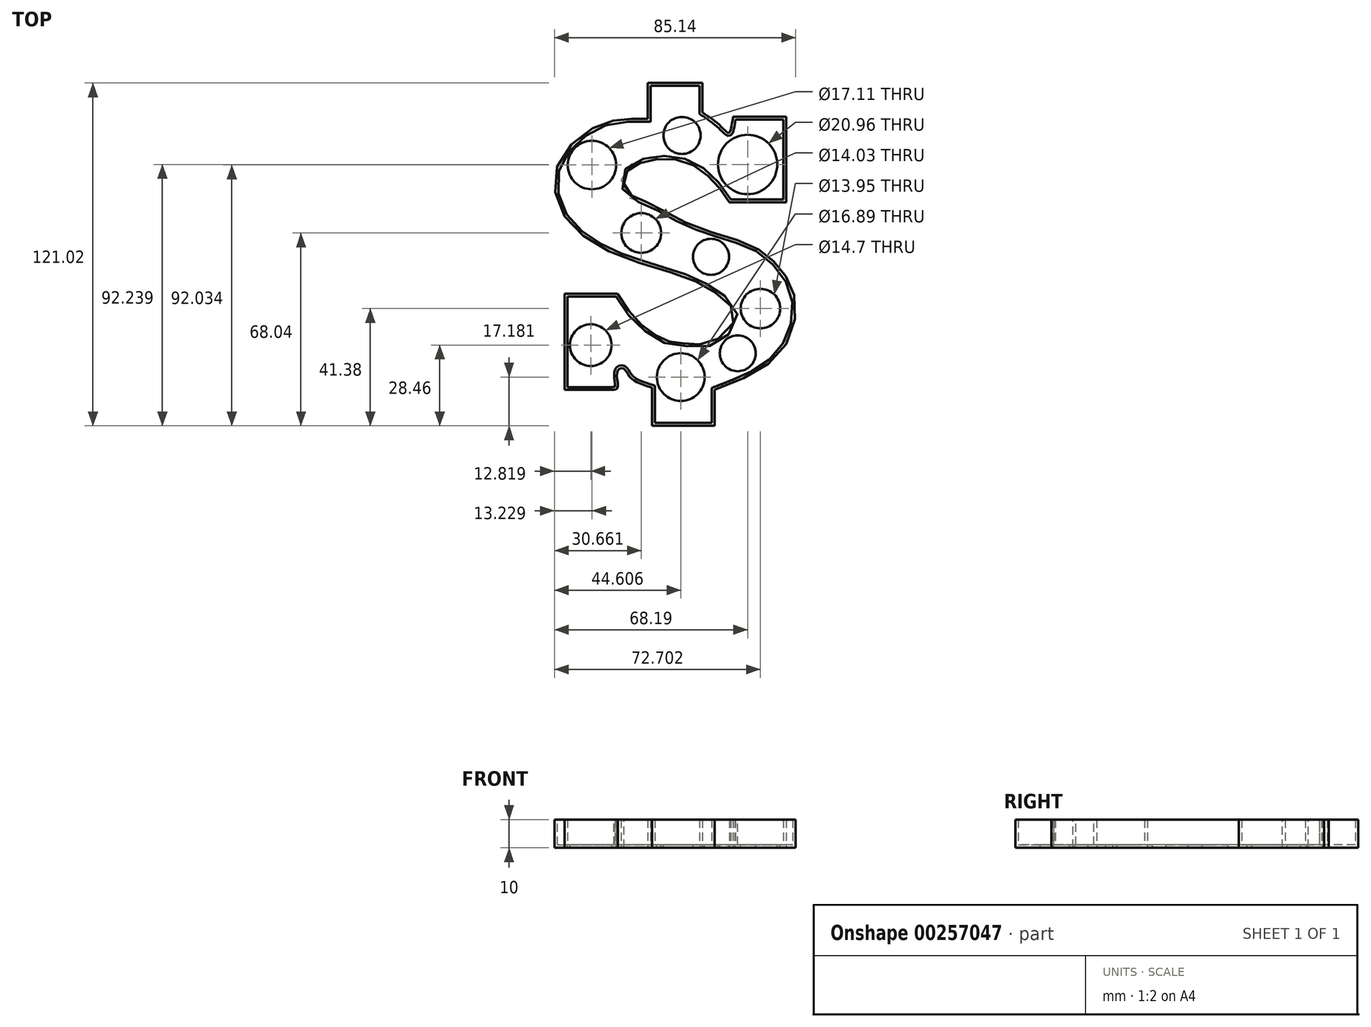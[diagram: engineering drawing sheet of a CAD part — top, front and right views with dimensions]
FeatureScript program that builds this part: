
annotation { "Feature Type Name" : "Feature", "Feature Type Description" : "" }
export const myFeature = defineFeature(function(context is Context, id is Id, definition is map)
    precondition{}
    {
        {
            var Q0;
            Q0=qCreatedBy(makeId("Top.planeOp"),FACE);
            var sketch = newSketch(context, id + "F0", { "sketchPlane" : qUnion([Q0])});
            skLineSegment(sketch, "E0", {"start": v(-8.22, 52.98) * mm, "end": v(11.07, 52.98) * mm});
            skLineSegment(sketch, "E1", {"start": v(11.07, 52.98) * mm, "end": v(11.07, 42.64) * mm});
            skLineSegment(sketch, "E2", {"start": v(-8.22, 52.98) * mm, "end": v(-8.22, 42.64) * mm});
            skLineSegment(sketch, "E3", {"start": v(21.96, 41) * mm, "end": v(40.65, 41) * mm});
            skLineSegment(sketch, "E4", {"start": v(40.65, 41) * mm, "end": v(40.65, 10.82) * mm});
            skLineSegment(sketch, "E5", {"start": v(40.65, 10.82) * mm, "end": v(20.61, 10.82) * mm});
            skLineSegment(sketch, "E6", {"start": v(-6.71, -54.62) * mm, "end": v(-6.71, -68.04) * mm});
            skLineSegment(sketch, "E7", {"start": v(-6.71, -68.04) * mm, "end": v(15.38, -68.04) * mm});
            skLineSegment(sketch, "E8", {"start": v(15.38, -68.04) * mm, "end": v(15.38, -55.37) * mm});
            skLineSegment(sketch, "E9", {"start": v(-20.87, -55.37) * mm, "end": v(-37.56, -55.37) * mm});
            skLineSegment(sketch, "E10", {"start": v(-37.56, -55.37) * mm, "end": v(-37.56, -21.41) * mm});
            skLineSegment(sketch, "E11", {"start": v(-37.56, -21.41) * mm, "end": v(-18.87, -21.41) * mm});
            skLineSegment(sketch, "E12", {"start": v(-8.22, 42.64) * mm, "end": v(-8.22, 40.28) * mm});
            skFitSpline(sketch, "E13", {"points": [v(-8.22, 40.28) * mm, v(-15.6, 40.28) * mm, v(-26.67, 37.56) * mm, v(-39.92, 24.13) * mm, v(-38.1, 6.9) * mm, v(-21.23, -6.71) * mm, v(4.9, -15.6) * mm, v(17.78, -22.5) * mm, v(22.5, -30.12) * mm, v(14.15, -38.65) * mm, v(5.8, -39.01) * mm, v(0, -38.47) * mm, v(-5.26, -36.1) * mm, v(-12.52, -30.3) * mm, v(-18.87, -21.41) * mm], "startDerivative": vector(-119.86, 3.94) * mm, "endDerivative": vector(-86.42, 138.88) * mm});
            skFitSpline(sketch, "E14", {"points": [v(11.07, 42.64) * mm, v(17.96, 37.38) * mm, v(20.5, 35.38) * mm, v(21.41, 37.92) * mm, v(21.96, 41) * mm], "startDerivative": vector(20.98, -14.44) * mm, "endDerivative": vector(2.34, 13.22) * mm});
            skFitSpline(sketch, "E15", {"points": [v(20.61, 10.82) * mm, v(15.04, 18.3) * mm, v(7.24, 24.26) * mm, v(-3.46, 26.25) * mm, v(-12.68, 23.9) * mm, v(-16.49, 19.82) * mm, v(-14.84, 13.96) * mm, v(-8.22, 10.82) * mm, v(7, 2.91) * mm, v(28.14, -4.28) * mm, v(37.94, -11.79) * mm, v(43.78, -23.23) * mm, v(38.5, -42.31) * mm, v(15.38, -55.37) * mm], "startDerivative": vector(-75.8, 124.36) * mm, "endDerivative": vector(-239.05, -90.17) * mm});
            skFitSpline(sketch, "E16", {"points": [v(-6.71, -54.62) * mm, v(-14.33, -50.99) * mm, v(-16.7, -47.9) * mm, v(-18.87, -48.63) * mm, v(-18.87, -54.62) * mm, v(-20.87, -55.37) * mm], "startDerivative": vector(-32.27, 10.38) * mm, "endDerivative": vector(-18.1, 0.06) * mm});
            skSolve(sketch);
        }
        {
            var Q0;
            Q0=makeQuery(id+"F0.imprint","IMPRINT",FACE,{"disambiguationData":[TD([[makeQuery(id+"F0.imprint","IMPRINT",EDGE,{"derivedFrom":sQuery(id+"F0.wireOp",EDGE,"E0")}),-1.0]])]});
            extrude(context, id + "F1", {"entities" : qUnion([Q0]), "depth" : 10 * mm});
        }
        {
            var Q0;
            Q0=makeQuery(id+"F1.opExtrude","CAP_FACE",FACE,{"disambiguationData":[OSD([sQuery(id+"F0.wireOp",EDGE,"E0"),sQuery(id+"F0.wireOp",EDGE,"E1"),sQuery(id+"F0.wireOp",EDGE,"E2"),sQuery(id+"F0.wireOp",EDGE,"E3"),sQuery(id+"F0.wireOp",EDGE,"E4"),sQuery(id+"F0.wireOp",EDGE,"E5"),sQuery(id+"F0.wireOp",EDGE,"E6"),sQuery(id+"F0.wireOp",EDGE,"E7"),sQuery(id+"F0.wireOp",EDGE,"E8"),sQuery(id+"F0.wireOp",EDGE,"E9"),sQuery(id+"F0.wireOp",EDGE,"E10"),sQuery(id+"F0.wireOp",EDGE,"E11"),sQuery(id+"F0.wireOp",EDGE,"E12"),sQuery(id+"F0.wireOp",EDGE,"E13"),sQuery(id+"F0.wireOp",EDGE,"E14"),sQuery(id+"F0.wireOp",EDGE,"E15"),sQuery(id+"F0.wireOp",EDGE,"E16")])],"isStart":false});
            shell(context, id + "F2", {"entities" : qUnion([Q0]), "thickness" : 1 * mm});
        }
        {
            var Q0;
            Q0=makeQuery(id+"F2.opShell","OFFSET_FACE",FACE,{"disambiguationData":[OSD([sQuery(id+"F0.wireOp",EDGE,"E0"),sQuery(id+"F0.wireOp",EDGE,"E1"),sQuery(id+"F0.wireOp",EDGE,"E2"),sQuery(id+"F0.wireOp",EDGE,"E3"),sQuery(id+"F0.wireOp",EDGE,"E4"),sQuery(id+"F0.wireOp",EDGE,"E5"),sQuery(id+"F0.wireOp",EDGE,"E6"),sQuery(id+"F0.wireOp",EDGE,"E7"),sQuery(id+"F0.wireOp",EDGE,"E8"),sQuery(id+"F0.wireOp",EDGE,"E9"),sQuery(id+"F0.wireOp",EDGE,"E10"),sQuery(id+"F0.wireOp",EDGE,"E11"),sQuery(id+"F0.wireOp",EDGE,"E12"),sQuery(id+"F0.wireOp",EDGE,"E13"),sQuery(id+"F0.wireOp",EDGE,"E14"),sQuery(id+"F0.wireOp",EDGE,"E15"),sQuery(id+"F0.wireOp",EDGE,"E16")])]});
            var sketch = newSketch(context, id + "F3", { "sketchPlane" : qUnion([Q0])});
            skCircle(sketch, "E17", {"center": v(27.07, 24.2) * mm, "radius": 10.48 * mm});
            skCircle(sketch, "E18", {"center": v(3.9, 34.45) * mm, "radius": 6.55 * mm});
            skCircle(sketch, "E19", {"center": v(-27.9, 24) * mm, "radius": 8.56 * mm});
            skCircle(sketch, "E20", {"center": v(-10.46, 0) * mm, "radius": 7.01 * mm});
            skCircle(sketch, "E21", {"center": v(14.15, -8.4) * mm, "radius": 6.37 * mm});
            skCircle(sketch, "E22", {"center": v(3.49, -50.86) * mm, "radius": 8.45 * mm});
            skCircle(sketch, "E23", {"center": v(23.58, -42.45) * mm, "radius": 6.33 * mm});
            skCircle(sketch, "E24", {"center": v(31.58, -26.66) * mm, "radius": 6.97 * mm});
            skCircle(sketch, "E25", {"center": v(-28.3, -39.58) * mm, "radius": 7.35 * mm});
            skSolve(sketch);
        }
        {
            var Q0;
            Q0=makeQuery(id+"F3.imprint","IMPRINT",FACE,{"disambiguationData":[TD([[makeQuery(id+"F3.imprint","IMPRINT",EDGE,{"derivedFrom":sQuery(id+"F3.wireOp",EDGE,"E19")}),1.0]])]});
            var Q1;
            Q1=makeQuery(id+"F3.imprint","IMPRINT",FACE,{"disambiguationData":[TD([[makeQuery(id+"F3.imprint","IMPRINT",EDGE,{"derivedFrom":sQuery(id+"F3.wireOp",EDGE,"E18")}),1.0]])]});
            var Q2;
            Q2=makeQuery(id+"F3.imprint","IMPRINT",FACE,{"disambiguationData":[TD([[makeQuery(id+"F3.imprint","IMPRINT",EDGE,{"derivedFrom":sQuery(id+"F3.wireOp",EDGE,"E17")}),1.0]])]});
            var Q3;
            Q3=makeQuery(id+"F3.imprint","IMPRINT",FACE,{"disambiguationData":[TD([[makeQuery(id+"F3.imprint","IMPRINT",EDGE,{"derivedFrom":sQuery(id+"F3.wireOp",EDGE,"E20")}),1.0]])]});
            var Q4;
            Q4=makeQuery(id+"F3.imprint","IMPRINT",FACE,{"disambiguationData":[TD([[makeQuery(id+"F3.imprint","IMPRINT",EDGE,{"derivedFrom":sQuery(id+"F3.wireOp",EDGE,"E21")}),1.0]])]});
            var Q5;
            Q5=makeQuery(id+"F3.imprint","IMPRINT",FACE,{"disambiguationData":[TD([[makeQuery(id+"F3.imprint","IMPRINT",EDGE,{"derivedFrom":sQuery(id+"F3.wireOp",EDGE,"E24")}),1.0]])]});
            var Q6;
            Q6=makeQuery(id+"F3.imprint","IMPRINT",FACE,{"disambiguationData":[TD([[makeQuery(id+"F3.imprint","IMPRINT",EDGE,{"derivedFrom":sQuery(id+"F3.wireOp",EDGE,"E23")}),1.0]])]});
            var Q7;
            Q7=makeQuery(id+"F3.imprint","IMPRINT",FACE,{"disambiguationData":[TD([[makeQuery(id+"F3.imprint","IMPRINT",EDGE,{"derivedFrom":sQuery(id+"F3.wireOp",EDGE,"E22")}),1.0]])]});
            var Q8;
            Q8=makeQuery(id+"F3.imprint","IMPRINT",FACE,{"disambiguationData":[TD([[makeQuery(id+"F3.imprint","IMPRINT",EDGE,{"derivedFrom":sQuery(id+"F3.wireOp",EDGE,"E25")}),1.0]])]});
            extrude(context, id + "F4", {"entities" : qUnion([Q0, Q1, Q2, Q3, Q4, Q5, Q6, Q7, Q8]), "operationType" : NewBodyOperationType.REMOVE, "oppositeDirection" : true, "depth" : 25 * mm});
        }
    });
